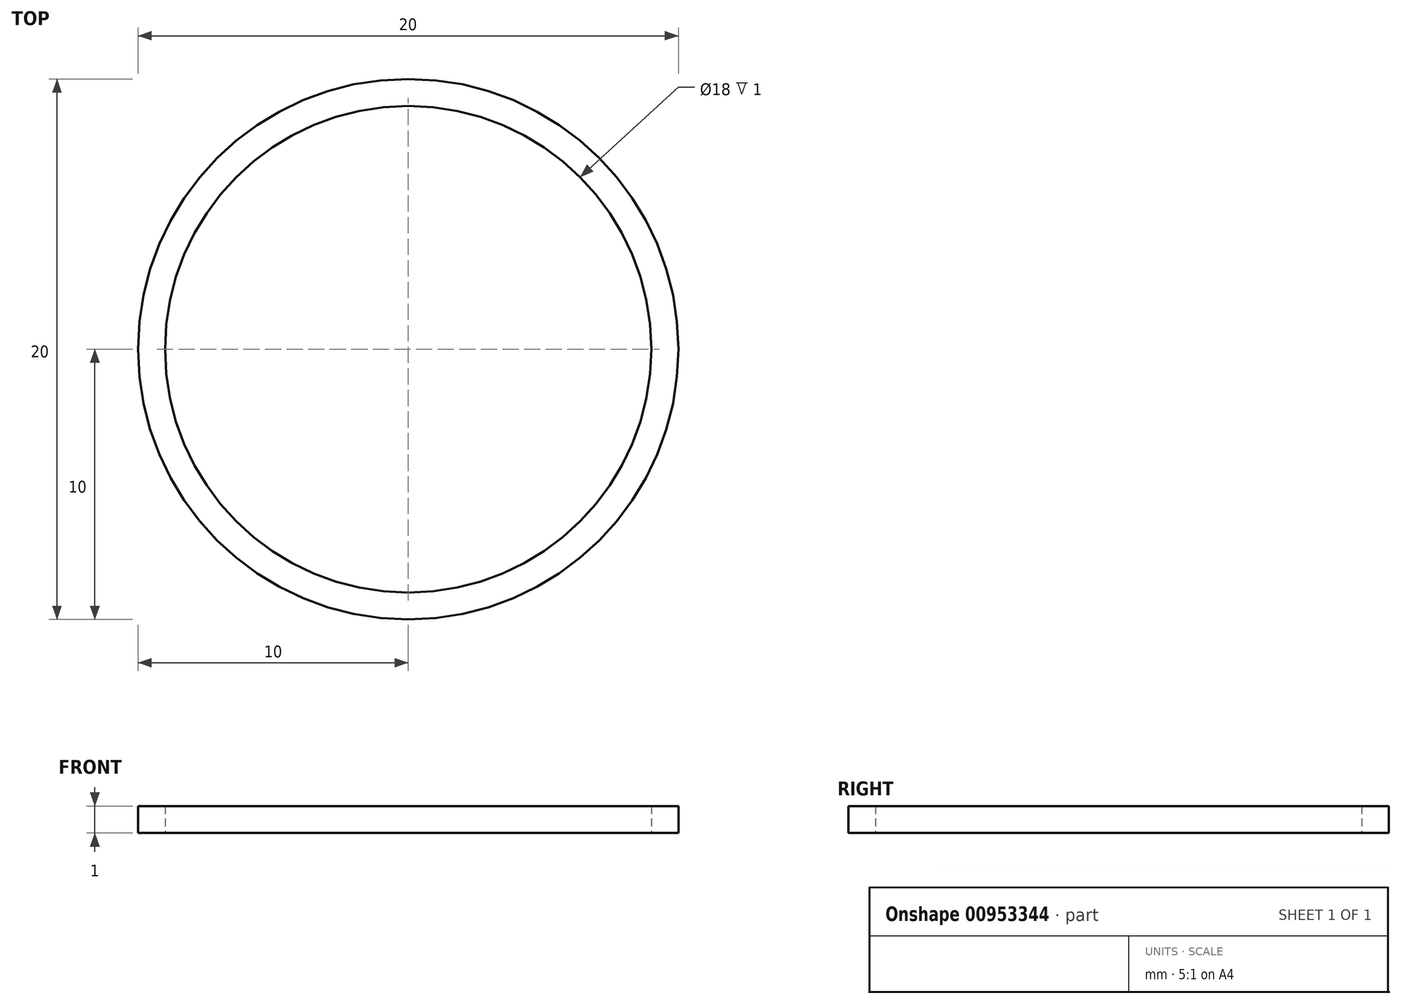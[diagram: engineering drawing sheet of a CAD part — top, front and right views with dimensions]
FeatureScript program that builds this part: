
annotation { "Feature Type Name" : "Feature", "Feature Type Description" : "" }
export const myFeature = defineFeature(function(context is Context, id is Id, definition is map)
    precondition{}
    {
        {
            var Q0;
            Q0=qCreatedBy(makeId("Top.planeOp"),FACE);
            var sketch = newSketch(context, id + "F0", { "sketchPlane" : qUnion([Q0])});
            skCircle(sketch, "E0", {"center": v(0, 0) * mm, "radius": 10 * mm});
            skCircle(sketch, "E1.0", {"center": v(0, 0) * mm, "radius": 9 * mm});
            skSolve(sketch);
        }
        {
            var Q0;
            Q0=qSketchRegion(id+"F0",true);
            extrude(context, id + "F1", {"entities" : qUnion([Q0]), "endBound" : BoundingType.SYMMETRIC, "depth" : 1 * mm, "offsetDistance" : 25 * mm});
        }
    });
